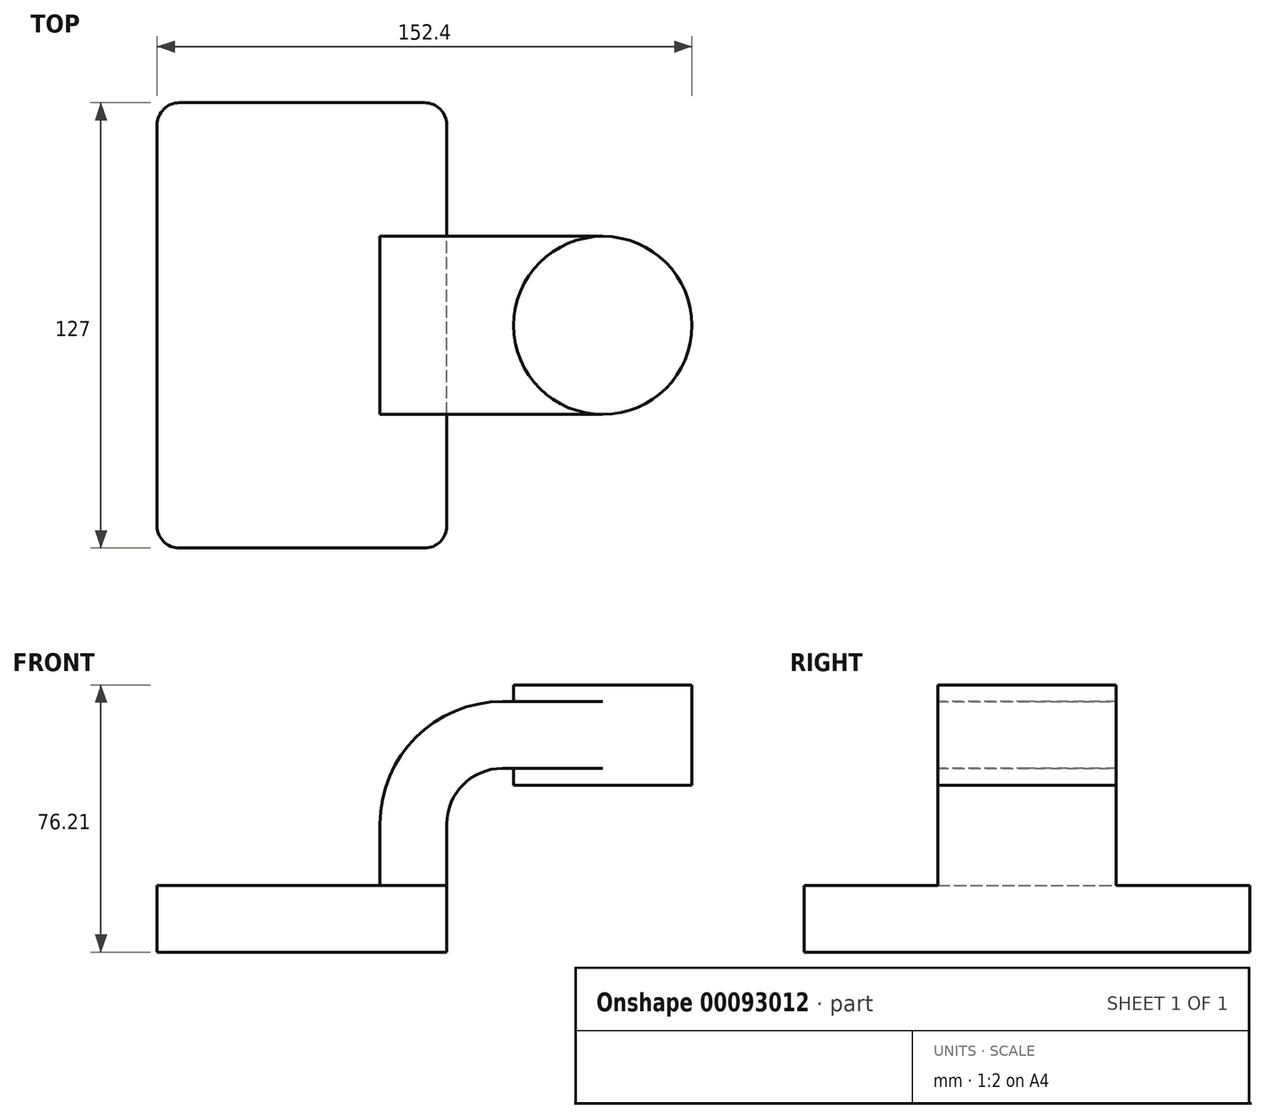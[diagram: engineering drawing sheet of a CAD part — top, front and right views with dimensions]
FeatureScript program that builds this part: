
annotation { "Feature Type Name" : "Feature", "Feature Type Description" : "" }
export const myFeature = defineFeature(function(context is Context, id is Id, definition is map)
    precondition{}
    {
        {
            var Q0;
            Q0=qCreatedBy(makeId("Front.planeOp"),FACE);
            var sketch = newSketch(context, id + "F0", { "sketchPlane" : qUnion([Q0])});
            skLineSegment(sketch, "E0.bottom", {"start": v(41.27, 9.53) * mm, "end": v(-41.28, 9.53) * mm});
            skLineSegment(sketch, "E0.top", {"start": v(41.28, -9.52) * mm, "end": v(-41.27, -9.52) * mm});
            skLineSegment(sketch, "E0.left", {"start": v(41.27, 9.53) * mm, "end": v(41.28, -9.52) * mm});
            skLineSegment(sketch, "E0.right", {"start": v(-41.28, 9.53) * mm, "end": v(-41.27, -9.52) * mm});
            skPoint(sketch, "E0.middle", {"position": v(0, 0) * mm});
            skLineSegment(sketch, "E1.bottom", {"start": v(111.12, 38.1) * mm, "end": v(60.33, 38.1) * mm});
            skLineSegment(sketch, "E1.top", {"start": v(111.12, 66.68) * mm, "end": v(60.33, 66.68) * mm});
            skLineSegment(sketch, "E1.left", {"start": v(111.12, 38.1) * mm, "end": v(111.12, 66.68) * mm});
            skLineSegment(sketch, "E1.right", {"start": v(60.33, 38.1) * mm, "end": v(60.33, 66.68) * mm});
            skPoint(sketch, "E1.middle", {"position": v(85.72, 52.39) * mm});
            skLineSegment(sketch, "E2", {"start": v(41.27, 9.53) * mm, "end": v(41.27, 27) * mm});
            skArc(sketch, "E3", {"start": v(41.27, 27) * mm, "mid": v(45.92, 38.23) * mm, "end": v(57.15, 42.88) * mm});
            skLineSegment(sketch, "E4", {"start": v(57.15, 42.88) * mm, "end": v(85.72, 42.88) * mm});
            skPoint(sketch, "E4.endSnap0", {"position": v(85.72, 38.1) * mm});
            skLineSegment(sketch, "E5.0", {"start": v(57.15, 61.93) * mm, "end": v(85.72, 61.93) * mm});
            skArc(sketch, "E5.1", {"start": v(22.22, 27) * mm, "mid": v(32.45, 51.7) * mm, "end": v(57.15, 61.93) * mm});
            skLineSegment(sketch, "E5.2", {"start": v(22.22, 9.53) * mm, "end": v(22.22, 27) * mm});
            skLineSegment(sketch, "E6", {"start": v(85.72, 38.1) * mm, "end": v(85.72, 66.68) * mm});
            skFitSpline(sketch, "E7", {"points": [v(-41.28, 9.53) * mm, v(57.15, 61.93) * mm], "startDerivative": vector(62.3, 98.61) * mm, "endDerivative": vector(171.45, -12.18) * mm});
            skSolve(sketch);
        }
        {
            var Q0;
            Q0=makeQuery(id+"F0.imprint","IMPRINT",FACE,{"disambiguationData":[TD([[makeQuery(id+"F0.imprint","IMPRINT",EDGE,{"derivedFrom":sQuery(id+"F0.wireOp",EDGE,"E0.top")}),-1.0]])]});
            extrude(context, id + "F1", {"entities" : qUnion([Q0]), "endBound" : BoundingType.SYMMETRIC, "depth" : 127 * mm});
        }
        {
            var Q0;
            {var subQ1=sQuery(id+"F0.wireOp",EDGE,"E2");Q0=makeQuery(id+"F0.imprint","IMPRINT",FACE,{"disambiguationData":[TD([[makeQuery(id+"F0.imprint","IMPRINT",EDGE,{"derivedFrom":subQ1}),1.0]])]});}
            extrude(context, id + "F2", {"entities" : qUnion([Q0]), "operationType" : NewBodyOperationType.ADD, "endBound" : BoundingType.SYMMETRIC, "depth" : 50.8 * mm});
        }
        {
            var Q0;
            Q0=makeQuery(id+"F0.imprint","IMPRINT",FACE,{"disambiguationData":[TD([[makeQuery(id+"F0.imprint","IMPRINT",EDGE,{"derivedFrom":sQuery(id+"F0.wireOp",EDGE,"E5.1")}),1.0]])]});
            extrude(context, id + "F3", {"entities" : qUnion([Q0]), "operationType" : NewBodyOperationType.ADD, "endBound" : BoundingType.SYMMETRIC, "depth" : 15.88 * mm});
        }
        {
            var Q0;
            {var subQ0=sQuery(id+"F0.wireOp",EDGE,"E4");var subQ1=sQuery(id+"F0.wireOp",EDGE,"E1.right");var subQ2=makeQuery(id+"F0.imprint","INTERSECT",VERTEX,{"derivedFrom":[subQ1,subQ0]});Q0=makeQuery(id+"F0.imprint","IMPRINT",FACE,{"disambiguationData":[TD([[makeQuery(id+"F0.imprint","IMPRINT",EDGE,{"disambiguationData":[TD([[subQ2,-1.0]])],"derivedFrom":subQ1}),-1.0]])]});}
            extrude(context, id + "F4", {"entities" : qUnion([Q0]), "operationType" : NewBodyOperationType.ADD, "endBound" : BoundingType.SYMMETRIC, "depth" : 50.8 * mm});
        }
        {
            var Q0;
            {var subQ0=sQuery(id+"F0.wireOp",EDGE,"E1.left");Q0=makeQuery(id+"F0.imprint","IMPRINT",FACE,{"disambiguationData":[TD([[makeQuery(id+"F0.imprint","IMPRINT",EDGE,{"derivedFrom":subQ0}),1.0]])]});}
            var Q1;
            Q1=sQuery(id+"F0.wireOp",EDGE,"E6");
            revolve(context, id + "F5", {"operationType" : NewBodyOperationType.ADD, "entities" : qUnion([Q0]), "axis" : qUnion([Q1]), "revolveType" : RevolveType.FULL});
        }
        {
            var Q0;
            Q0=makeQuery(id+"F1.opExtrude","CAP_EDGE",EDGE,{"disambiguationData":[OSD([sQuery(id+"F0.wireOp",EDGE,"E0.left")])],"isStart":false});
            var Q1;
            Q1=makeQuery(id+"F1.opExtrude","CAP_EDGE",EDGE,{"disambiguationData":[OSD([sQuery(id+"F0.wireOp",EDGE,"E0.right")])],"isStart":false});
            var Q2;
            Q2=makeQuery(id+"F1.opExtrude","CAP_EDGE",EDGE,{"disambiguationData":[OSD([sQuery(id+"F0.wireOp",EDGE,"E0.right")])],"isStart":true});
            var Q3;
            Q3=makeQuery(id+"F1.opExtrude","CAP_EDGE",EDGE,{"disambiguationData":[OSD([sQuery(id+"F0.wireOp",EDGE,"E0.left")])],"isStart":true});
            fillet(context, id + "F6", {"entities" : qUnion([Q0, Q1, Q2, Q3]), "radius" : 6.35 * mm, "tangentPropagation" : true, "allowEdgeOverflow" : false});
        }
    });
